# Revit family: Furniture_Stools_Sjobergs_Stool
name_source: partatom
category: Furniture
revit_build: Autodesk Revit 2017 (Build: 20190508_0315(x64)
units: mm (PartAtom-declared; Revit-internal decimal feet)

## family parameters
Always vertical = Yes
Cut with Voids When Loaded = No
OmniClass Number = 23.40.20.14.14.11
OmniClass Title = Chairs
Room Calculation Point = No
Shared = No
Work Plane-Based = No

## types (1)
- 33520 Stool
    AssetType = Movable
    BIMObjectName = Furniture_Stools_Sjobergs_Stool
    Brand = Sjöbergs
    Category = School, woodwork
    ChairMainMaterial = Beech
    ChairSecondaryMaterial = Cork
    Color = Wooden
    ConvergoRefNr = 0184-2005-0018-SE
    Cost = 0 $
    DurationUnit = Year
    EANNumber = 7316703520107
    Features = Stackable.
    Finish = Solid varnished birch. Seat in cork.
    HighestSeatingHeight = 500 mm
    IfcExportAs = IfcFurnishingElementType
    IfcExportType = CHAIR
    LowestSeatingHeight = 500 mm
    MainColor = Wooden
    Manufacturer = Sjöbergs
    ManufacturerName = Sjöbergs
    ManufacturerURL = https://www.sjobergs.se
    Material = Wood, cork.
    Model = 33520 Stool
    ModelReference = 33520
    NBSDescription = Domestic chairs
    NBSReference = 45-35-20/365
    Name = Sjobergs_Stool
    NominalDepth = 430 mm  [stored 1.41076 ft]
    NominalHeight = 500 mm
    NominalLength = 430 mm  [stored 1.41076 ft]
    SeatingHeight = 500 mm
    Shape = Sculptured
    Size = 430x430x500 mm
    URL = https://www.sjobergs.se
    Uniclass2 = Pr_40_50_12_83
    Uniclass2015Description = Foot stools
    Uniclass2015Reference = Pr_40_50_51_31
    Version = 1
    VersionDate = 26/06/2020
    WarrantyDurationUnit = Year
    Weight = 3.0 kg

note: [stored X ft] marks values corroborated as IEEE doubles in the binary element streams (Revit-internal decimal feet)

## geometry (parser evidence)
native form markers: Sweep x6
no freeform markers — native parametric forms only
